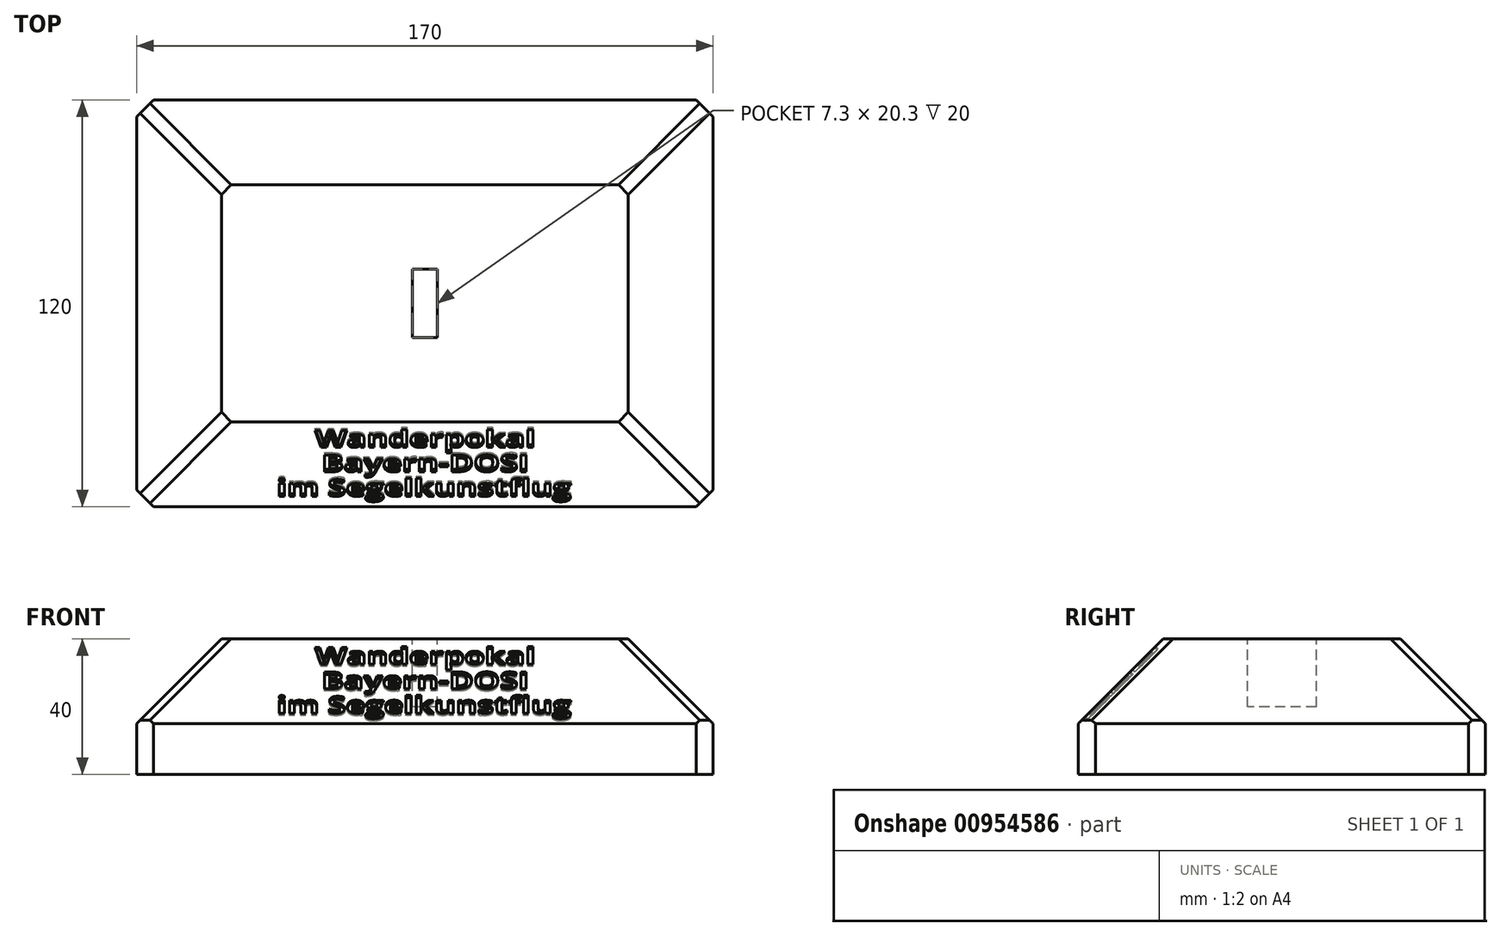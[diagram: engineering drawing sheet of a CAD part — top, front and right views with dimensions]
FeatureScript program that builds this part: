
annotation { "Feature Type Name" : "Feature", "Feature Type Description" : "" }
export const myFeature = defineFeature(function(context is Context, id is Id, definition is map)
    precondition{}
    {
        {
            var Q0;
            Q0=qCreatedBy(makeId("Top.planeOp"),FACE);
            var sketch = newSketch(context, id + "F0", { "sketchPlane" : qUnion([Q0])});
            skLineSegment(sketch, "E0", {"start": v(0, -82.2) * mm, "end": v(0, 103.78) * mm, "construction": true});
            skPoint(sketch, "E1.end.orphan", {"position": v(-170.75, 0) * mm});
            skLineSegment(sketch, "E2", {"start": v(-67.95, 0) * mm, "end": v(78.68, 0) * mm, "construction": true});
            skLineSegment(sketch, "E3.bottom", {"start": v(-85, 60) * mm, "end": v(85, 60) * mm});
            skLineSegment(sketch, "E3.top", {"start": v(-85, -60) * mm, "end": v(85, -60) * mm});
            skLineSegment(sketch, "E3.left", {"start": v(-85, 60) * mm, "end": v(-85, -60) * mm});
            skLineSegment(sketch, "E3.right", {"start": v(85, 60) * mm, "end": v(85, -60) * mm});
            skSolve(sketch);
        }
        {
            var Q0;
            Q0=makeQuery(id+"F0.imprint","IMPRINT",FACE,{"disambiguationData":[TD([[makeQuery(id+"F0.imprint","IMPRINT",EDGE,{"derivedFrom":sQuery(id+"F0.wireOp",EDGE,"E3.bottom")}),-1.0]])]});
            extrude(context, id + "F1", {"entities" : qUnion([Q0]), "depth" : 40 * mm, "offsetDistance" : 25 * mm});
        }
        {
            var Q0;
            Q0=makeQuery(id+"F1.opExtrude","CAP_FACE",FACE,{"disambiguationData":[OSD([sQuery(id+"F0.wireOp",EDGE,"E3.bottom"),sQuery(id+"F0.wireOp",EDGE,"E3.top"),sQuery(id+"F0.wireOp",EDGE,"E3.left"),sQuery(id+"F0.wireOp",EDGE,"E3.right")])],"isStart":false});
            chamfer(context, id + "F2", {"entities" : qUnion([Q0]), "width" : 25 * mm, "tangentPropagation" : true});
        }
        {
            var Q0;
            Q0=makeQuery(id+"F1.opExtrude","SWEPT_EDGE",EDGE,{"disambiguationData":[OSD([sQuery(id+"F0.wireOp",EDGE,"E3.top"),sQuery(id+"F0.wireOp",EDGE,"E3.left")])]});
            var Q1;
            Q1=makeQuery(id+"F1.opExtrude","SWEPT_EDGE",EDGE,{"disambiguationData":[OSD([sQuery(id+"F0.wireOp",EDGE,"E3.bottom"),sQuery(id+"F0.wireOp",EDGE,"E3.left")])]});
            var Q2;
            Q2=makeQuery(id+"F1.opExtrude","SWEPT_EDGE",EDGE,{"disambiguationData":[OSD([sQuery(id+"F0.wireOp",EDGE,"E3.top"),sQuery(id+"F0.wireOp",EDGE,"E3.right")])]});
            var Q3;
            Q3=makeQuery(id+"F1.opExtrude","SWEPT_EDGE",EDGE,{"disambiguationData":[OSD([sQuery(id+"F0.wireOp",EDGE,"E3.bottom"),sQuery(id+"F0.wireOp",EDGE,"E3.right")])]});
            chamfer(context, id + "F3", {"entities" : qUnion([Q0, Q1, Q2, Q3]), "width" : 5 * mm, "tangentPropagation" : true});
        }
        {
            var Q0;
            Q0=makeQuery(id+"F2.opChamfer","BLEND_FACE",FACE,{"disambiguationData":[OSD([sQuery(id+"F0.wireOp",EDGE,"E3.top")])]});
            var sketch = newSketch(context, id + "F4", { "sketchPlane" : qUnion([Q0])});
            skText(sketch, "E4", { "text": "Wanderpokal\nBayrische Doppelsitzermeisterschaft \nim Kunstflug", "fontName": "OpenSans-Regular.ttf"});
            const initialGuessF4  = {"E4": [-0.62988, -0.01414, 1, 0, 0.02828]};
            skSetInitialGuess(sketch, initialGuessF4);
            skSolve(sketch);
        }
        {
            var Q0;
            Q0=makeQuery(id+"F2.opChamfer","BLEND_FACE",FACE,{"disambiguationData":[OSD([sQuery(id+"F0.wireOp",EDGE,"E3.top")])]});
            cPlane(context, id + "F5", {"entities" : qUnion([Q0]), "cplaneType" : CPlaneType.OFFSET, "offset" : 0 * mm, "width" : 150 * mm, "height" : 150 * mm});
        }
        {
            var Q0;
            Q0=qCreatedBy(id+"F5.planeOp",FACE);
            var sketch = newSketch(context, id + "F6", { "sketchPlane" : qUnion([Q0])});
            skText(sketch, "E5", { "text": "Wanderpokal", "fontName": "OpenSans-Bold.ttf"});
            skText(sketch, "E6", { "text": "\nBayern-DOSI", "fontName": "OpenSans-Bold.ttf"});
            skText(sketch, "E7", { "text": "\n\nim Segelkunstflug", "fontName": "OpenSans-Bold.ttf"});
            const initialGuessF6  = {"E5": [-0.03244, -0.007, 1, 0, 0.007], "E6": [-0.03044, -0.004, 1, 0, 0.007], "E7": [-0.04367, -0.001, 1, 0, 0.007]};
            skSetInitialGuess(sketch, initialGuessF6);
            skSolve(sketch);
        }
        {
            var Q0;
            Q0 = qSketchRegion(id + "F6", true);
            extrude(context, id + "F7", {"entities" : qUnion([Q0]), "operationType" : NewBodyOperationType.REMOVE, "oppositeDirection" : true, "depth" : 1 * mm, "offsetDistance" : 25 * mm});
        }
        {
            var Q0;
            Q0=makeQuery(id+"F1.opExtrude","CAP_FACE",FACE,{"disambiguationData":[OSD([sQuery(id+"F0.wireOp",EDGE,"E3.bottom"),sQuery(id+"F0.wireOp",EDGE,"E3.top"),sQuery(id+"F0.wireOp",EDGE,"E3.left"),sQuery(id+"F0.wireOp",EDGE,"E3.right")])],"isStart":false});
            var sketch = newSketch(context, id + "F8", { "sketchPlane" : qUnion([Q0])});
            skLineSegment(sketch, "E8.left", {"start": v(-2.26, 0) * mm, "end": v(-2.26, 0) * mm});
            skLineSegment(sketch, "E8.right", {"start": v(2.68, 0) * mm, "end": v(2.68, 0) * mm});
            skLineSegment(sketch, "E9.bottom", {"start": v(3.65, 10.15) * mm, "end": v(-3.65, 10.15) * mm});
            skLineSegment(sketch, "E9.top", {"start": v(3.65, -10.15) * mm, "end": v(-3.65, -10.15) * mm});
            skLineSegment(sketch, "E9.left", {"start": v(3.65, 10.15) * mm, "end": v(3.65, -10.15) * mm});
            skLineSegment(sketch, "E9.right", {"start": v(-3.65, 10.15) * mm, "end": v(-3.65, -10.15) * mm});
            skPoint(sketch, "E9.middle", {"position": v(0, 0) * mm});
            skSolve(sketch);
        }
        {
            var Q0;
            Q0=makeQuery(id+"F8.imprint","IMPRINT",FACE,{"disambiguationData":[TD([[makeQuery(id+"F8.imprint","IMPRINT",EDGE,{"derivedFrom":sQuery(id+"F8.wireOp",EDGE,"E9.bottom")}),1.0]])]});
            extrude(context, id + "F9", {"entities" : qUnion([Q0]), "operationType" : NewBodyOperationType.REMOVE, "oppositeDirection" : true, "depth" : 20 * mm, "offsetDistance" : 25 * mm});
        }
        {
            var Q0;
            Q0=makeQuery(id+"F2.opChamfer","BLEND_EDGE",EDGE,{"blendedFrom":[makeQuery(id+"F1.opExtrude","CAP_EDGE",EDGE,{"disambiguationData":[OSD([sQuery(id+"F0.wireOp",EDGE,"E3.top")])],"isStart":false}),makeQuery(id+"F1.opExtrude","CAP_EDGE",EDGE,{"disambiguationData":[OSD([sQuery(id+"F0.wireOp",EDGE,"E3.left")])],"isStart":false})],"blendedInto":[]});
            var Q1;
            Q1=makeQuery(id+"F2.opChamfer","BLEND_EDGE",EDGE,{"blendedFrom":[makeQuery(id+"F1.opExtrude","CAP_EDGE",EDGE,{"disambiguationData":[OSD([sQuery(id+"F0.wireOp",EDGE,"E3.top")])],"isStart":false}),makeQuery(id+"F1.opExtrude","CAP_EDGE",EDGE,{"disambiguationData":[OSD([sQuery(id+"F0.wireOp",EDGE,"E3.right")])],"isStart":false})],"blendedInto":[]});
            var Q2;
            Q2=makeQuery(id+"F2.opChamfer","BLEND_EDGE",EDGE,{"blendedFrom":[makeQuery(id+"F1.opExtrude","CAP_EDGE",EDGE,{"disambiguationData":[OSD([sQuery(id+"F0.wireOp",EDGE,"E3.bottom")])],"isStart":false}),makeQuery(id+"F1.opExtrude","CAP_EDGE",EDGE,{"disambiguationData":[OSD([sQuery(id+"F0.wireOp",EDGE,"E3.left")])],"isStart":false})],"blendedInto":[]});
            var Q3;
            Q3=makeQuery(id+"F2.opChamfer","BLEND_EDGE",EDGE,{"blendedFrom":[makeQuery(id+"F1.opExtrude","CAP_EDGE",EDGE,{"disambiguationData":[OSD([sQuery(id+"F0.wireOp",EDGE,"E3.bottom")])],"isStart":false}),makeQuery(id+"F1.opExtrude","CAP_EDGE",EDGE,{"disambiguationData":[OSD([sQuery(id+"F0.wireOp",EDGE,"E3.right")])],"isStart":false})],"blendedInto":[]});
            chamfer(context, id + "F10", {"entities" : qUnion([Q0, Q1, Q2, Q3]), "width" : 4.1 * mm, "tangentPropagation" : true});
        }
    });
